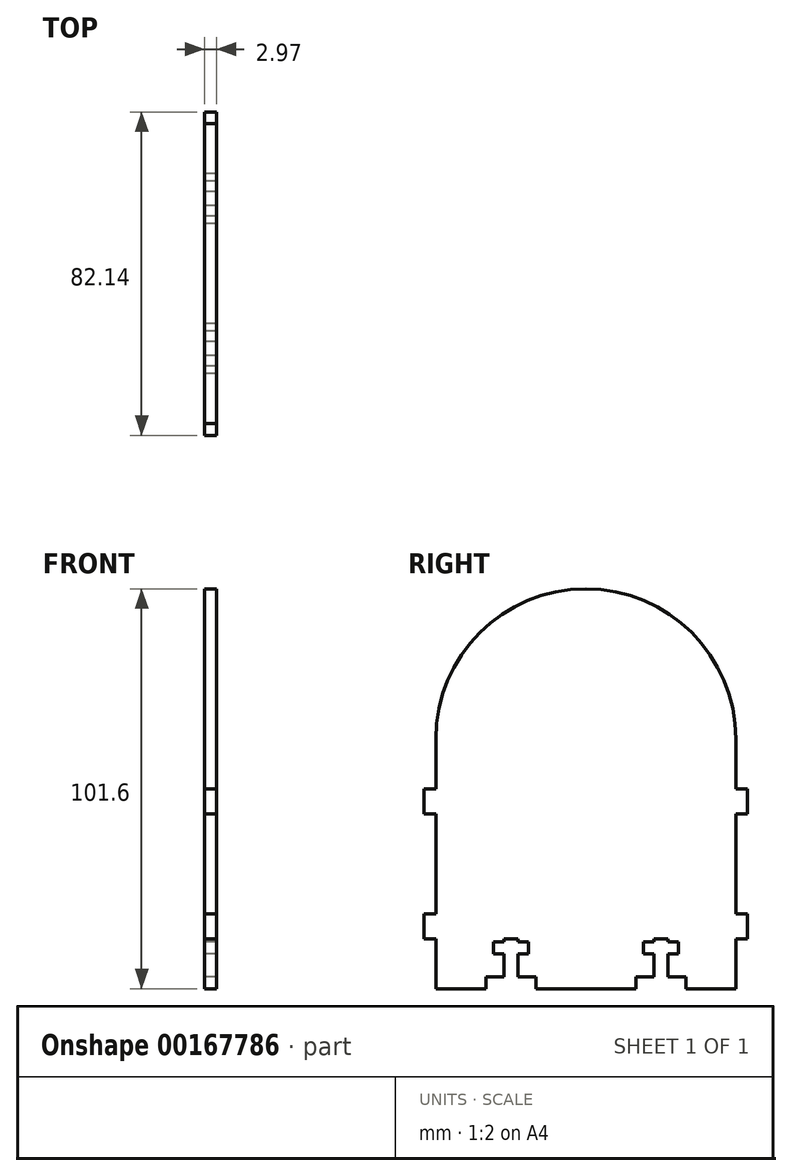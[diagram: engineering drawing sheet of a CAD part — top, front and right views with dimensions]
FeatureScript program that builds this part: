
annotation { "Feature Type Name" : "Feature", "Feature Type Description" : "" }
export const myFeature = defineFeature(function(context is Context, id is Id, definition is map)
    precondition{}
    {
        {
            var Q0;
            Q0=qCreatedBy(makeId("Right.planeOp"),FACE);
            var sketch = newSketch(context, id + "F0", { "sketchPlane" : qUnion([Q0])});
            skLineSegment(sketch, "E0.bottom", {"start": v(38.1, 31.75) * mm, "end": v(-38.1, 31.75) * mm});
            skLineSegment(sketch, "E0.top", {"start": v(38.1, -31.75) * mm, "end": v(-38.1, -31.75) * mm});
            skLineSegment(sketch, "E0.left", {"start": v(38.1, 31.75) * mm, "end": v(38.1, 19.05) * mm});
            skLineSegment(sketch, "E0.right", {"start": v(-38.1, 31.75) * mm, "end": v(-38.1, -12.7) * mm});
            skPoint(sketch, "E0.middle", {"position": v(0, 0) * mm});
            skArc(sketch, "E1", {"start": v(38.1, 31.75) * mm, "mid": v(0, 69.85) * mm, "end": v(-38.1, 31.75) * mm});
            skLineSegment(sketch, "E2", {"start": v(0, 31.75) * mm, "end": v(0, -31.75) * mm, "construction": true});
            skLineSegment(sketch, "E3", {"start": v(-38.1, 0) * mm, "end": v(38.1, 0) * mm, "construction": true});
            skLineSegment(sketch, "E4.bottom", {"start": v(-38.1, 19.05) * mm, "end": v(-41.07, 19.05) * mm});
            skLineSegment(sketch, "E4.top", {"start": v(-38.1, 12.7) * mm, "end": v(-41.07, 12.7) * mm});
            skLineSegment(sketch, "E4.right", {"start": v(-41.07, 19.05) * mm, "end": v(-41.07, 12.7) * mm});
            skLineSegment(sketch, "E5.MirrorCS", {"start": v(-41.07, -19.05) * mm, "end": v(-41.07, -12.7) * mm});
            skLineSegment(sketch, "E6.MirrorCS", {"start": v(-38.1, -19.05) * mm, "end": v(-41.07, -19.05) * mm});
            skLineSegment(sketch, "E7.MirrorCS", {"start": v(-38.1, -12.7) * mm, "end": v(-41.07, -12.7) * mm});
            skLineSegment(sketch, "E8.MirrorCS", {"start": v(38.1, 12.7) * mm, "end": v(41.07, 12.7) * mm});
            skLineSegment(sketch, "E9.MirrorCS", {"start": v(41.07, 19.05) * mm, "end": v(41.07, 12.7) * mm});
            skLineSegment(sketch, "E10.MirrorCS", {"start": v(38.1, 19.05) * mm, "end": v(41.07, 19.05) * mm});
            skLineSegment(sketch, "E11.MirrorCS", {"start": v(38.1, -12.7) * mm, "end": v(41.07, -12.7) * mm});
            skLineSegment(sketch, "E12.MirrorCS", {"start": v(41.07, -19.05) * mm, "end": v(41.07, -12.7) * mm});
            skLineSegment(sketch, "E13.MirrorCS", {"start": v(38.1, -19.05) * mm, "end": v(41.07, -19.05) * mm});
            skLineSegment(sketch, "E14.bottom", {"start": v(-25.4, -31.75) * mm, "end": v(-12.7, -31.75) * mm});
            skLineSegment(sketch, "E14.top", {"start": v(-25.4, -28.78) * mm, "end": v(-20.83, -28.78) * mm});
            skLineSegment(sketch, "E14.left", {"start": v(-25.4, -31.75) * mm, "end": v(-25.4, -28.78) * mm});
            skLineSegment(sketch, "E14.right", {"start": v(-12.7, -31.75) * mm, "end": v(-12.7, -28.78) * mm});
            skLineSegment(sketch, "E15.bottom", {"start": v(-20.83, -31.75) * mm, "end": v(-17.27, -31.75) * mm});
            skLineSegment(sketch, "E15.top", {"start": v(-20.83, -19.05) * mm, "end": v(-17.27, -19.05) * mm});
            skLineSegment(sketch, "E15.left", {"start": v(-20.83, -28.78) * mm, "end": v(-20.83, -22.97) * mm});
            skLineSegment(sketch, "E15.right", {"start": v(-17.27, -28.78) * mm, "end": v(-17.27, -22.97) * mm});
            skLineSegment(sketch, "E16", {"start": v(-19.05, -28.78) * mm, "end": v(-19.05, -31.75) * mm, "construction": true});
            skLineSegment(sketch, "E17", {"start": v(-19.05, -19.05) * mm, "end": v(-19.05, -28.78) * mm, "construction": true});
            skLineSegment(sketch, "E18.bottom", {"start": v(-14.6, -22.97) * mm, "end": v(-17.27, -22.97) * mm});
            skLineSegment(sketch, "E18.top", {"start": v(-14.6, -19.92) * mm, "end": v(-17.27, -19.92) * mm});
            skLineSegment(sketch, "E18.left", {"start": v(-14.6, -22.97) * mm, "end": v(-14.6, -19.92) * mm});
            skLineSegment(sketch, "E18.right", {"start": v(-23.5, -22.97) * mm, "end": v(-23.5, -19.92) * mm});
            skPoint(sketch, "E18.middle", {"position": v(-19.05, -21.44) * mm});
            skLineSegment(sketch, "E19.MirrorCS", {"start": v(20.83, -28.78) * mm, "end": v(20.83, -22.97) * mm});
            skLineSegment(sketch, "E20.MirrorCS", {"start": v(17.27, -28.78) * mm, "end": v(17.27, -22.97) * mm});
            skLineSegment(sketch, "E21.MirrorCS", {"start": v(25.4, -28.78) * mm, "end": v(20.83, -28.78) * mm});
            skLineSegment(sketch, "E22.MirrorCS", {"start": v(12.7, -31.75) * mm, "end": v(12.7, -28.78) * mm});
            skLineSegment(sketch, "E23.MirrorCS", {"start": v(25.4, -31.75) * mm, "end": v(25.4, -28.78) * mm});
            skLineSegment(sketch, "E24.MirrorCS", {"start": v(14.6, -19.92) * mm, "end": v(17.27, -19.92) * mm});
            skLineSegment(sketch, "E25.MirrorCS", {"start": v(14.6, -22.97) * mm, "end": v(17.27, -22.97) * mm});
            skLineSegment(sketch, "E26.MirrorCS", {"start": v(23.5, -22.97) * mm, "end": v(23.5, -19.92) * mm});
            skLineSegment(sketch, "E27.MirrorCS", {"start": v(14.6, -22.97) * mm, "end": v(14.6, -19.92) * mm});
            skLineSegment(sketch, "E28.MirrorCS", {"start": v(20.83, -19.05) * mm, "end": v(17.27, -19.05) * mm});
            skLineSegment(sketch, "E29.trimOffspring", {"start": v(38.1, -19.05) * mm, "end": v(38.1, -31.75) * mm});
            skLineSegment(sketch, "E30.trimOffspring", {"start": v(38.1, 12.7) * mm, "end": v(38.1, -12.7) * mm});
            skLineSegment(sketch, "E31.trimOffspring", {"start": v(-38.1, -19.05) * mm, "end": v(-38.1, -31.75) * mm});
            skLineSegment(sketch, "E32.trimOffspring", {"start": v(-20.83, -19.92) * mm, "end": v(-20.83, -19.05) * mm});
            skLineSegment(sketch, "E33.trimOffspring", {"start": v(-17.27, -19.92) * mm, "end": v(-17.27, -19.05) * mm});
            skLineSegment(sketch, "E34.trimOffspring", {"start": v(17.27, -19.92) * mm, "end": v(17.27, -19.05) * mm});
            skLineSegment(sketch, "E35.trimOffspring", {"start": v(20.83, -19.92) * mm, "end": v(20.83, -19.05) * mm});
            skLineSegment(sketch, "E36.trimOffspring", {"start": v(20.83, -19.92) * mm, "end": v(23.5, -19.92) * mm});
            skLineSegment(sketch, "E37.trimOffspring", {"start": v(20.83, -22.97) * mm, "end": v(23.5, -22.97) * mm});
            skLineSegment(sketch, "E38.trimOffspring", {"start": v(-20.83, -19.92) * mm, "end": v(-23.5, -19.92) * mm});
            skLineSegment(sketch, "E39.trimOffspring", {"start": v(-20.83, -22.97) * mm, "end": v(-23.5, -22.97) * mm});
            skPoint(sketch, "E40.orphan", {"position": v(17.27, -31.75) * mm});
            skLineSegment(sketch, "E41.trimOffspring", {"start": v(17.27, -28.78) * mm, "end": v(12.7, -28.78) * mm});
            skPoint(sketch, "E42.orphan", {"position": v(20.83, -31.75) * mm});
            skLineSegment(sketch, "E43.trimOffspring", {"start": v(-17.27, -28.78) * mm, "end": v(-12.7, -28.78) * mm});
            skPoint(sketch, "E44.orphan", {"position": v(-19.05, -31.75) * mm});
            skSolve(sketch);
        }
        {
            var Q0;
            {var subQ34=sQuery(id+"F0.wireOp",EDGE,"E0.bottom");Q0=makeQuery(id+"F0.imprint","IMPRINT",FACE,{"disambiguationData":[TD([[makeQuery(id+"F0.imprint","IMPRINT",EDGE,{"derivedFrom":subQ34}),1.0]])]});}
            var Q1;
            Q1=makeQuery(id+"F0.imprint","IMPRINT",FACE,{"disambiguationData":[TD([[makeQuery(id+"F0.imprint","IMPRINT",EDGE,{"derivedFrom":sQuery(id+"F0.wireOp",EDGE,"E0.bottom")}),-1.0]])]});
            var Q2;
            Q2=makeQuery(id+"F0.imprint","IMPRINT",FACE,{"disambiguationData":[TD([[makeQuery(id+"F0.imprint","IMPRINT",EDGE,{"derivedFrom":sQuery(id+"F0.wireOp",EDGE,"E4.bottom")}),1.0]])]});
            var Q3;
            Q3=makeQuery(id+"F0.imprint","IMPRINT",FACE,{"disambiguationData":[TD([[makeQuery(id+"F0.imprint","IMPRINT",EDGE,{"derivedFrom":sQuery(id+"F0.wireOp",EDGE,"E5.MirrorCS")}),-1.0]])]});
            var Q4;
            {var subQ0=sQuery(id+"F0.wireOp",EDGE,"E8.MirrorCS");Q4=makeQuery(id+"F0.imprint","IMPRINT",FACE,{"disambiguationData":[TD([[makeQuery(id+"F0.imprint","IMPRINT",EDGE,{"derivedFrom":subQ0}),1.0]])]});}
            var Q5;
            {var subQ0=sQuery(id+"F0.wireOp",EDGE,"E11.MirrorCS");Q5=makeQuery(id+"F0.imprint","IMPRINT",FACE,{"disambiguationData":[TD([[makeQuery(id+"F0.imprint","IMPRINT",EDGE,{"derivedFrom":subQ0}),-1.0]])]});}
            extrude(context, id + "F1", {"entities" : qUnion([Q0, Q1, Q2, Q3, Q4, Q5]), "depth" : 2.97 * mm});
        }
    });
